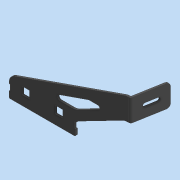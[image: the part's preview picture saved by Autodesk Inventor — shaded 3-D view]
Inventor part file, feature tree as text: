
AUTODESK INVENTOR PART (.ipt)
format: ipt  version: 2020 (Build 240168000, 168)  size: 388,096 bytes
history: native  units: mm
features: other x3, extrude x1, plane x1
ambient origin geometry x8: Origin, YZ Plane, XZ Plane, XY Plane, X Axis, Y Axis, Z Axis, Center Point
bodies: Body1 (feature_tree)
feature tree (5):
  other  "實體1"
  extrude  "擠出1"  Depth=130.0mm
  other  "折彎零件1"
  plane  "工作平面1"
  other  "定義1"
